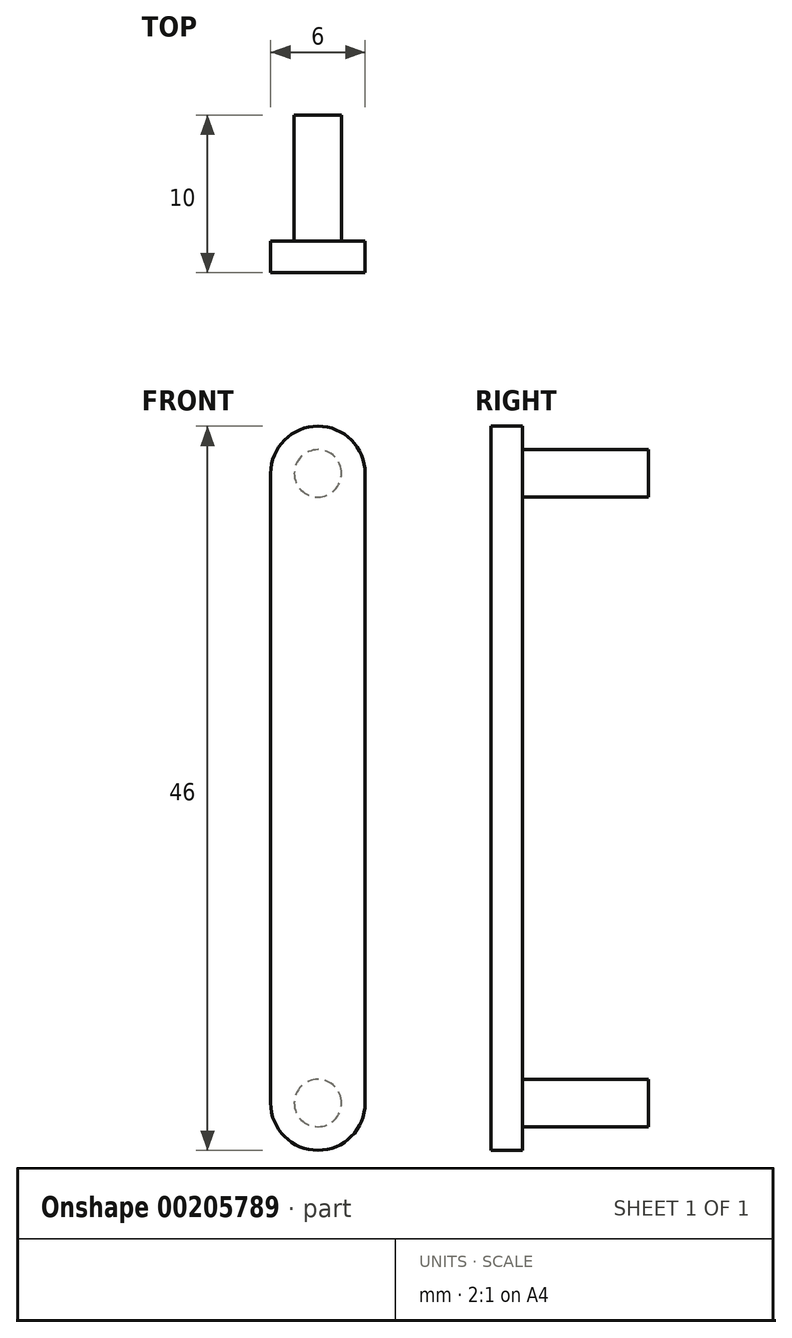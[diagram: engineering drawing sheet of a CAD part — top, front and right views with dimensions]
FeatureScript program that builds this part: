
annotation { "Feature Type Name" : "Feature", "Feature Type Description" : "" }
export const myFeature = defineFeature(function(context is Context, id is Id, definition is map)
    precondition{}
    {
        {
            var Q0;
            Q0=qCreatedBy(makeId("Front.planeOp"),FACE);
            var sketch = newSketch(context, id + "F0", { "sketchPlane" : qUnion([Q0])});
            skCircle(sketch, "E0", {"center": v(0, 0) * mm, "radius": 1.5 * mm});
            skSolve(sketch);
        }
        {
            var Q0;
            Q0 = qSketchRegion(id + "F0", true);
            extrude(context, id + "F1", {"entities" : qUnion([Q0]), "oppositeDirection" : true, "depth" : 10 * mm});
        }
        {
            var Q0;
            Q0=qCreatedBy(makeId("Front.planeOp"),FACE);
            var sketch = newSketch(context, id + "F2", { "sketchPlane" : qUnion([Q0])});
            skLineSegment(sketch, "E1", {"start": v(0, 0) * mm, "end": v(0, -40) * mm});
            skArc(sketch, "E2.0.startCap", {"start": v(-3, 0) * mm, "mid": v(0, 3) * mm, "end": v(3, 0) * mm});
            skArc(sketch, "E2.0.endCap", {"start": v(3, -40) * mm, "mid": v(0, -43) * mm, "end": v(-3, -40) * mm});
            skLineSegment(sketch, "E2.0.left", {"start": v(3, 0) * mm, "end": v(3, -40) * mm});
            skLineSegment(sketch, "E2.0.right", {"start": v(-3, 0) * mm, "end": v(-3, -40) * mm});
            skSolve(sketch);
        }
        {
            var Q0;
            Q0=qCreatedBy(makeId("Front.planeOp"),FACE);
            var sketch = newSketch(context, id + "F3", { "sketchPlane" : qUnion([Q0])});
            skCircle(sketch, "E3", {"center": v(0, -40) * mm, "radius": 1.5 * mm});
            skSolve(sketch);
        }
        {
            var Q0;
            Q0 = qSketchRegion(id + "F3", true);
            var Q1;
            Q1=makeQuery(id+"F1.opExtrude","CAP_FACE",FACE,{"disambiguationData":[OSD([sQuery(id+"F0.wireOp",EDGE,"E0")])],"isStart":false});
            extrude(context, id + "F4", {"entities" : qUnion([Q0]), "endBound" : BoundingType.UP_TO_SURFACE, "oppositeDirection" : true, "endBoundEntityFace" : qUnion([Q1]), "depth" : 25 * mm});
        }
        {
            var Q0;
            Q0 = qSketchRegion(id + "F2", true);
            extrude(context, id + "F5", {"entities" : qUnion([Q0]), "operationType" : NewBodyOperationType.ADD, "oppositeDirection" : true, "depth" : 2 * mm});
        }
    });
